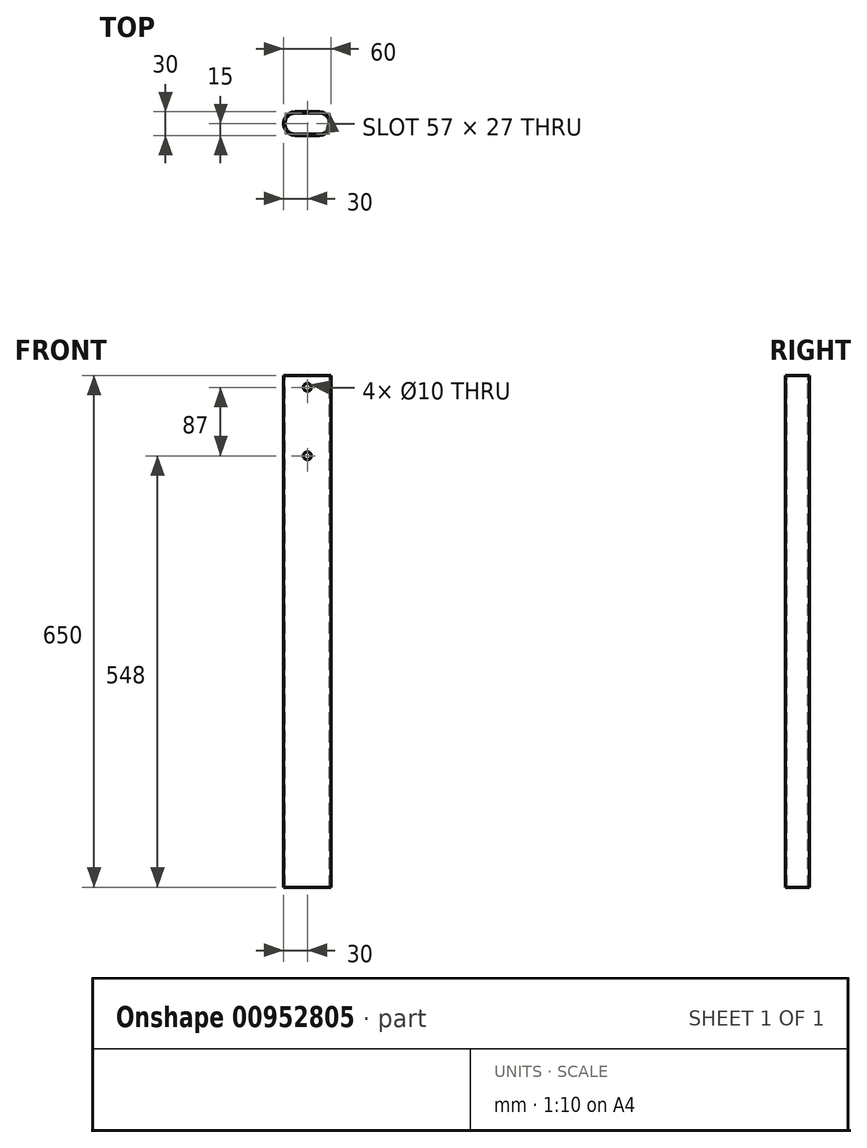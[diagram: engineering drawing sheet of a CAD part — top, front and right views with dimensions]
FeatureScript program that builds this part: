
annotation { "Feature Type Name" : "Feature", "Feature Type Description" : "" }
export const myFeature = defineFeature(function(context is Context, id is Id, definition is map)
    precondition{}
    {
        {
            var Q0;
            Q0=qCreatedBy(makeId("Top.planeOp"),FACE);
            var sketch = newSketch(context, id + "F0", { "sketchPlane" : qUnion([Q0])});
            skLineSegment(sketch, "E0.bottom", {"start": v(-15, 15) * mm, "end": v(15, 15) * mm});
            skLineSegment(sketch, "E0.top", {"start": v(-15, -15) * mm, "end": v(15, -15) * mm});
            skLineSegment(sketch, "E0.left", {"start": v(-30, 0) * mm, "end": v(-30, 0) * mm});
            skLineSegment(sketch, "E0.right", {"start": v(30, 0) * mm, "end": v(30, 0) * mm});
            skPoint(sketch, "E0.middle", {"position": v(0, 0) * mm});
            skPoint(sketch, "E1.visualSharp", {"position": v(-30, 15) * mm});
            skArc(sketch, "E1.filletArc", {"start": v(-15, 15) * mm, "mid": v(-25.6, 10.6) * mm, "end": v(-30, 0) * mm});
            skPoint(sketch, "E2.visualSharp", {"position": v(-30, -15) * mm});
            skArc(sketch, "E2.filletArc", {"start": v(-30, 0) * mm, "mid": v(-25.6, -10.6) * mm, "end": v(-15, -15) * mm});
            skPoint(sketch, "E3.visualSharp", {"position": v(30, -15) * mm});
            skArc(sketch, "E3.filletArc", {"start": v(15, -15) * mm, "mid": v(25.6, -10.6) * mm, "end": v(30, 0) * mm});
            skPoint(sketch, "E4.visualSharp", {"position": v(30, 15) * mm});
            skArc(sketch, "E4.filletArc", {"start": v(30, 0) * mm, "mid": v(25.6, 10.6) * mm, "end": v(15, 15) * mm});
            skLineSegment(sketch, "E5.bottom", {"start": v(-15, 13.5) * mm, "end": v(15, 13.5) * mm});
            skLineSegment(sketch, "E5.top", {"start": v(-15, -13.5) * mm, "end": v(15, -13.5) * mm});
            skLineSegment(sketch, "E5.left", {"start": v(-28.5, 0) * mm, "end": v(-28.5, 0) * mm});
            skLineSegment(sketch, "E5.right", {"start": v(28.5, 0) * mm, "end": v(28.5, 0) * mm});
            skPoint(sketch, "E6.visualSharp", {"position": v(-28.5, 13.5) * mm});
            skArc(sketch, "E6.filletArc", {"start": v(-15, 13.5) * mm, "mid": v(-24.55, 9.55) * mm, "end": v(-28.5, 0) * mm});
            skPoint(sketch, "E7.visualSharp", {"position": v(-28.5, -13.5) * mm});
            skArc(sketch, "E7.filletArc", {"start": v(-28.5, 0) * mm, "mid": v(-24.55, -9.55) * mm, "end": v(-15, -13.5) * mm});
            skPoint(sketch, "E8.visualSharp", {"position": v(28.5, -13.5) * mm});
            skArc(sketch, "E8.filletArc", {"start": v(15, -13.5) * mm, "mid": v(24.55, -9.55) * mm, "end": v(28.5, 0) * mm});
            skPoint(sketch, "E9.visualSharp", {"position": v(28.5, 13.5) * mm});
            skArc(sketch, "E9.filletArc", {"start": v(28.5, 0) * mm, "mid": v(24.55, 9.55) * mm, "end": v(15, 13.5) * mm});
            skSolve(sketch);
        }
        {
            var Q0;
            Q0=qSketchRegion(id+"F0",true);
            extrude(context, id + "F1", {"entities" : qUnion([Q0]), "oppositeDirection" : true, "depth" : 650 * mm, "offsetDistance" : 25 * mm});
        }
        {
            var Q0;
            Q0=makeQuery(id+"F1.opExtrude","SWEPT_FACE",FACE,{"disambiguationData":[OSD([sQuery(id+"F0.wireOp",EDGE,"E0.bottom")])]});
            var sketch = newSketch(context, id + "F2", { "sketchPlane" : qUnion([Q0])});
            skLineSegment(sketch, "E10.0", {"start": v(15, 0) * mm, "end": v(-15, 0) * mm, "construction": true});
            skLineSegment(sketch, "E11", {"start": v(0, 0) * mm, "end": v(0, -15) * mm, "construction": true});
            skCircle(sketch, "E12", {"center": v(0, -15) * mm, "radius": 5 * mm});
            skLineSegment(sketch, "E13", {"start": v(0, -15) * mm, "end": v(0, -102) * mm, "construction": true});
            skCircle(sketch, "E14", {"center": v(0, -102) * mm, "radius": 5 * mm});
            skSolve(sketch);
        }
        {
            var Q0;
            Q0=makeQuery(id+"F2.imprint","IMPRINT",FACE,{"disambiguationData":[TD([[makeQuery(id+"F2.imprint","IMPRINT",EDGE,{"derivedFrom":sQuery(id+"F2.wireOp",EDGE,"E12")}),1.0]])]});
            var Q1;
            Q1=makeQuery(id+"F2.imprint","IMPRINT",FACE,{"disambiguationData":[TD([[makeQuery(id+"F2.imprint","IMPRINT",EDGE,{"derivedFrom":sQuery(id+"F2.wireOp",EDGE,"E14")}),1.0]])]});
            extrude(context, id + "F3", {"entities" : qUnion([Q0, Q1]), "operationType" : NewBodyOperationType.REMOVE, "oppositeDirection" : true, "depth" : 40 * mm, "offsetDistance" : 25 * mm});
        }
    });
